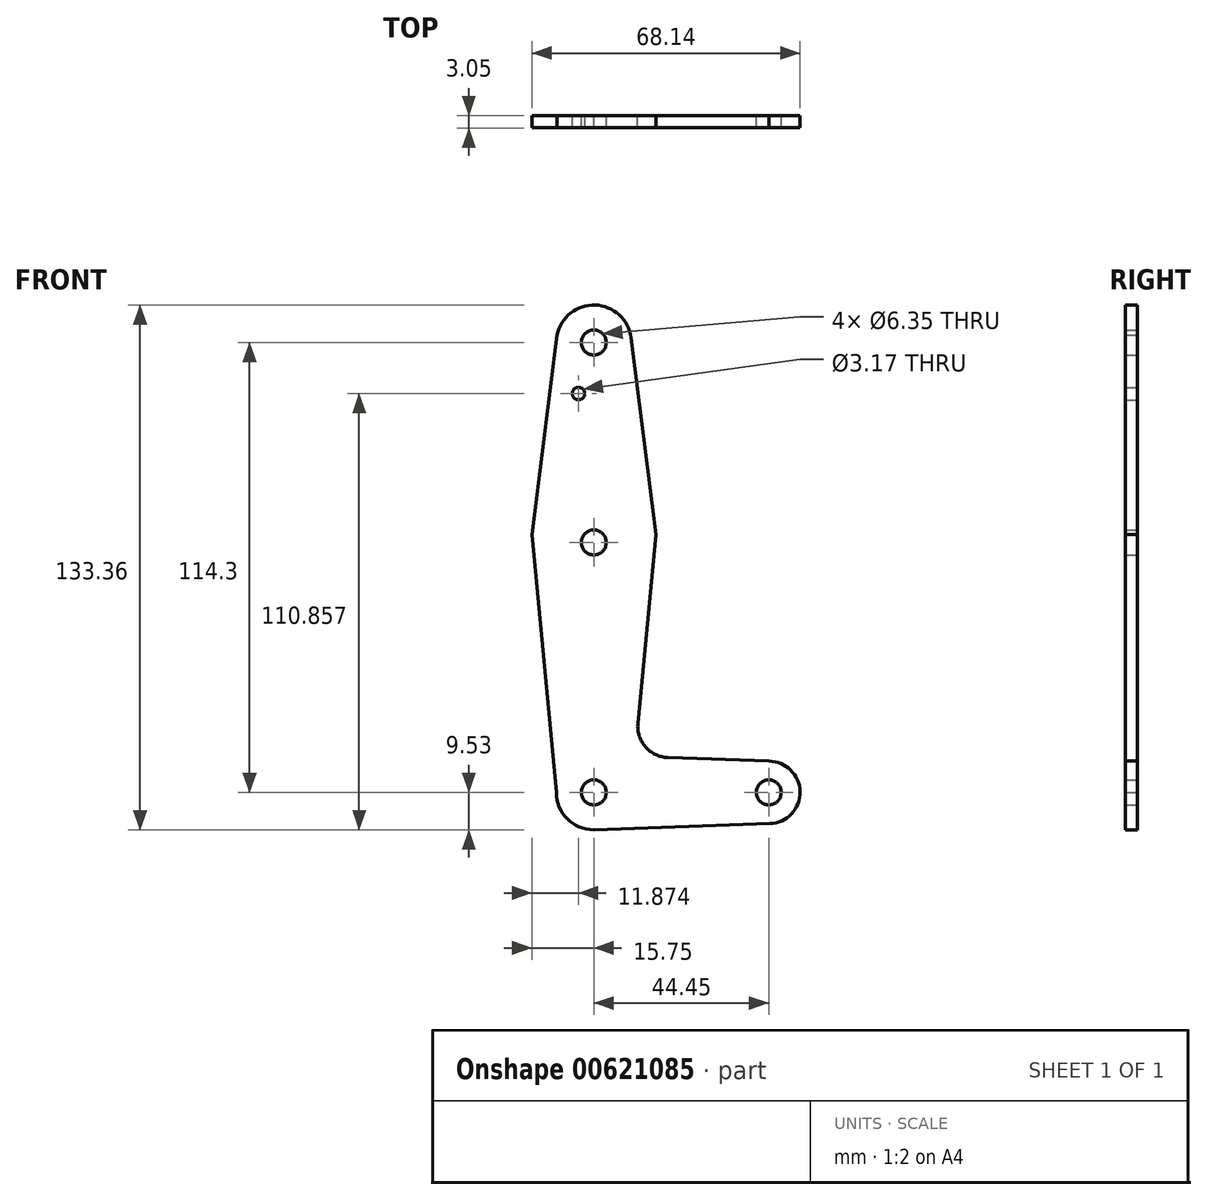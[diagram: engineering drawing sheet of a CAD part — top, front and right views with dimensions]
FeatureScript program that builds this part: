
annotation { "Feature Type Name" : "Feature", "Feature Type Description" : "" }
export const myFeature = defineFeature(function(context is Context, id is Id, definition is map)
    precondition{}
    {
        {
            var Q0;
            Q0=qCreatedBy(makeId("Front.planeOp"),FACE);
            var sketch = newSketch(context, id + "F0", { "sketchPlane" : qUnion([Q0])});
            skLineSegment(sketch, "E0", {"start": v(0, 0) * mm, "end": v(0, 114.3) * mm});
            skLineSegment(sketch, "E1", {"start": v(0, 0) * mm, "end": v(44.45, 0) * mm});
            skCircle(sketch, "E2", {"center": v(0, 63.5) * mm, "radius": 15.88 * mm});
            skCircle(sketch, "E3", {"center": v(0, 0) * mm, "radius": 9.53 * mm});
            skCircle(sketch, "E4", {"center": v(44.45, 0) * mm, "radius": 1.51 * mm});
            skCircle(sketch, "E5", {"center": v(44.45, 0) * mm, "radius": 7.94 * mm});
            skCircle(sketch, "E6", {"center": v(0, 114.3) * mm, "radius": 9.53 * mm});
            skLineSegment(sketch, "E7", {"start": v(-9.33, 116.22) * mm, "end": v(-15.75, 65.5) * mm});
            skLineSegment(sketch, "E8", {"start": v(-9.52, 0) * mm, "end": v(-15.75, 65.5) * mm});
            skLineSegment(sketch, "E9", {"start": v(15.75, 65.48) * mm, "end": v(11.2, 17.55) * mm});
            skLineSegment(sketch, "E10", {"start": v(9.45, 115.52) * mm, "end": v(15.75, 65.48) * mm});
            skLineSegment(sketch, "E11", {"start": v(0, -9.53) * mm, "end": v(44.73, -7.93) * mm});
            skLineSegment(sketch, "E12", {"start": v(44.45, 7.94) * mm, "end": v(18.82, 8.86) * mm});
            skPoint(sketch, "E13.newPointA", {"position": v(0, 9.53) * mm});
            skArc(sketch, "E13.filletArc", {"start": v(11.2, 17.55) * mm, "mid": v(13.13, 11.56) * mm, "end": v(18.82, 8.86) * mm});
            skCircle(sketch, "E14", {"center": v(0, 114.3) * mm, "radius": 3.18 * mm});
            skCircle(sketch, "E15", {"center": v(0, 63.5) * mm, "radius": 3.18 * mm});
            skCircle(sketch, "E16", {"center": v(0, 0) * mm, "radius": 3.18 * mm});
            skCircle(sketch, "E17", {"center": v(44.45, 0) * mm, "radius": 3.18 * mm});
            skCircle(sketch, "E18", {"center": v(-3.88, 101.33) * mm, "radius": 1.59 * mm});
            skSolve(sketch);
        }
        {
            var Q0;
            Q0=makeQuery(id+"F0.imprint","IMPRINT",FACE,{"disambiguationData":[TD([[makeQuery(id+"F0.imprint","IMPRINT",EDGE,{"derivedFrom":sQuery(id+"F0.wireOp",EDGE,"E18")}),-1.0]])]});
            var Q1;
            Q1=makeQuery(id+"F0.imprint","IMPRINT",FACE,{"disambiguationData":[TD([[makeQuery(id+"F0.imprint","IMPRINT",EDGE,{"derivedFrom":sQuery(id+"F0.wireOp",EDGE,"E14")}),-1.0]])]});
            var Q2;
            {var subQ5=sQuery(id+"F0.wireOp",EDGE,"E10");Q2=makeQuery(id+"F0.imprint","IMPRINT",FACE,{"disambiguationData":[TD([[makeQuery(id+"F0.imprint","IMPRINT",EDGE,{"derivedFrom":subQ5}),-1.0]])]});}
            var Q3;
            {var subQ1=sQuery(id+"F0.wireOp",EDGE,"E2");var subQ3=sQuery(id+"F0.wireOp",EDGE,"E0");var subQ4=makeQuery(id+"F0.imprint","INTERSECT",VERTEX,{"disambiguationData":[OD(0.0)],"derivedFrom":[subQ3,subQ1]});Q3=makeQuery(id+"F0.imprint","IMPRINT",FACE,{"disambiguationData":[TD([[makeQuery(id+"F0.imprint","IMPRINT",EDGE,{"disambiguationData":[TD([[subQ4,-1.0]])],"derivedFrom":subQ3}),-1.0]])]});}
            var Q4;
            {var subQ1=sQuery(id+"F0.wireOp",EDGE,"E2");var subQ3=sQuery(id+"F0.wireOp",EDGE,"E0");var subQ8=makeQuery(id+"F0.imprint","INTERSECT",VERTEX,{"disambiguationData":[OD(0.0)],"derivedFrom":[subQ3,subQ1]});Q4=makeQuery(id+"F0.imprint","IMPRINT",FACE,{"disambiguationData":[TD([[makeQuery(id+"F0.imprint","IMPRINT",EDGE,{"disambiguationData":[TD([[subQ8,-1.0]])],"derivedFrom":subQ3}),1.0]])]});}
            var Q5;
            {var subQ0=sQuery(id+"F0.wireOp",EDGE,"E3");var subQ1=sQuery(id+"F0.wireOp",EDGE,"E0");var subQ2=makeQuery(id+"F0.imprint","INTERSECT",VERTEX,{"derivedFrom":[subQ1,subQ0]});Q5=makeQuery(id+"F0.imprint","IMPRINT",FACE,{"disambiguationData":[TD([[makeQuery(id+"F0.imprint","IMPRINT",EDGE,{"disambiguationData":[TD([[subQ2,-1.0]])],"derivedFrom":subQ1}),1.0]])]});}
            var Q6;
            {var subQ5=sQuery(id+"F0.wireOp",EDGE,"E12");Q6=makeQuery(id+"F0.imprint","IMPRINT",FACE,{"disambiguationData":[TD([[makeQuery(id+"F0.imprint","IMPRINT",EDGE,{"derivedFrom":subQ5}),1.0]])]});}
            var Q7;
            {var subQ0=sQuery(id+"F0.wireOp",EDGE,"E5");var subQ1=sQuery(id+"F0.wireOp",EDGE,"E1");var subQ2=makeQuery(id+"F0.imprint","INTERSECT",VERTEX,{"derivedFrom":[subQ1,subQ0]});Q7=makeQuery(id+"F0.imprint","IMPRINT",FACE,{"disambiguationData":[TD([[makeQuery(id+"F0.imprint","IMPRINT",EDGE,{"disambiguationData":[TD([[subQ2,1.0]])],"derivedFrom":subQ1}),-1.0]])]});}
            var Q8;
            {var subQ0=sQuery(id+"F0.wireOp",EDGE,"E16");var subQ1=sQuery(id+"F0.wireOp",EDGE,"E0");var subQ2=makeQuery(id+"F0.imprint","INTERSECT",VERTEX,{"derivedFrom":[subQ1,subQ0]});Q8=makeQuery(id+"F0.imprint","IMPRINT",FACE,{"disambiguationData":[TD([[makeQuery(id+"F0.imprint","IMPRINT",EDGE,{"disambiguationData":[TD([[subQ2,-1.0]])],"derivedFrom":subQ1}),-1.0]])]});}
            var Q9;
            {var subQ2=sQuery(id+"F0.wireOp",EDGE,"E0");var subQ6=sQuery(id+"F0.wireOp",EDGE,"E16");var subQ10=makeQuery(id+"F0.imprint","INTERSECT",VERTEX,{"derivedFrom":[subQ2,subQ6]});Q9=makeQuery(id+"F0.imprint","IMPRINT",FACE,{"disambiguationData":[TD([[makeQuery(id+"F0.imprint","IMPRINT",EDGE,{"disambiguationData":[TD([[subQ10,-1.0]])],"derivedFrom":subQ2}),1.0]])]});}
            var Q10;
            Q10=makeQuery(id+"F0.imprint","IMPRINT",FACE,{"disambiguationData":[TD([[makeQuery(id+"F0.imprint","IMPRINT",EDGE,{"derivedFrom":sQuery(id+"F0.wireOp",EDGE,"E17")}),-1.0]])]});
            extrude(context, id + "F1", {"entities" : qUnion([Q0, Q1, Q2, Q3, Q4, Q5, Q6, Q7, Q8, Q9, Q10]), "depth" : 3.05 * mm, "offsetDistance" : 25.4 * mm});
        }
    });
